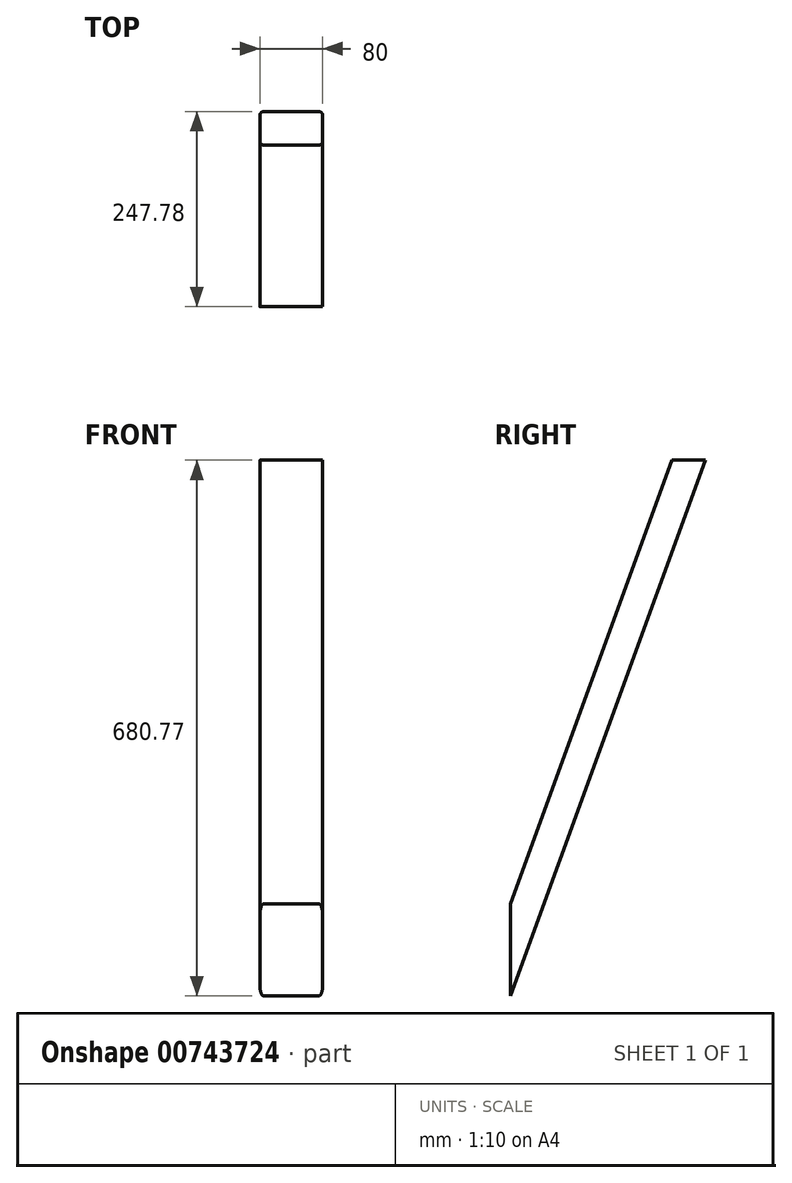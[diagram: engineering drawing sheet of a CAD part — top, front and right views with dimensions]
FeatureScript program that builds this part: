
annotation { "Feature Type Name" : "Feature", "Feature Type Description" : "" }
export const myFeature = defineFeature(function(context is Context, id is Id, definition is map)
    precondition{}
    {
        {
            var Q0;
            Q0=qCreatedBy(makeId("Right.planeOp"),FACE);
            var sketch = newSketch(context, id + "F0", { "sketchPlane" : qUnion([Q0])});
            skLineSegment(sketch, "E0", {"start": v(0, 0) * mm, "end": v(0, 116.95) * mm});
            skLineSegment(sketch, "E1", {"start": v(0, 116.95) * mm, "end": v(205.21, 680.77) * mm});
            skLineSegment(sketch, "E2", {"start": v(205.21, 680.77) * mm, "end": v(247.78, 680.77) * mm});
            skLineSegment(sketch, "E3", {"start": v(0, 0) * mm, "end": v(247.78, 680.77) * mm});
            skSolve(sketch);
        }
        {
            var Q0;
            Q0=makeQuery(id+"F0.imprint","IMPRINT",FACE,{"disambiguationData":[TD([[makeQuery(id+"F0.imprint","IMPRINT",EDGE,{"derivedFrom":sQuery(id+"F0.wireOp",EDGE,"E0")}),-1.0]])]});
            extrude(context, id + "F1", {"entities" : qUnion([Q0]), "depth" : 80 * mm, "offsetDistance" : 25 * mm});
        }
        {
            var Q0;
            Q0=makeQuery(id+"F1.opExtrude","CAP_EDGE",EDGE,{"disambiguationData":[OSD([sQuery(id+"F0.wireOp",EDGE,"E3")])],"isStart":false});
            var Q1;
            Q1=makeQuery(id+"F1.opExtrude","CAP_EDGE",EDGE,{"disambiguationData":[OSD([sQuery(id+"F0.wireOp",EDGE,"E1")])],"isStart":false});
            var Q2;
            Q2=makeQuery(id+"F1.opExtrude","CAP_EDGE",EDGE,{"disambiguationData":[OSD([sQuery(id+"F0.wireOp",EDGE,"E1")])],"isStart":true});
            var Q3;
            Q3=makeQuery(id+"F1.opExtrude","CAP_EDGE",EDGE,{"disambiguationData":[OSD([sQuery(id+"F0.wireOp",EDGE,"E3")])],"isStart":true});
            fillet(context, id + "F2", {"entities" : qUnion([Q0, Q1, Q2, Q3]), "radius" : 5 * mm, "tangentPropagation" : true, "allowEdgeOverflow" : false});
        }
    });
